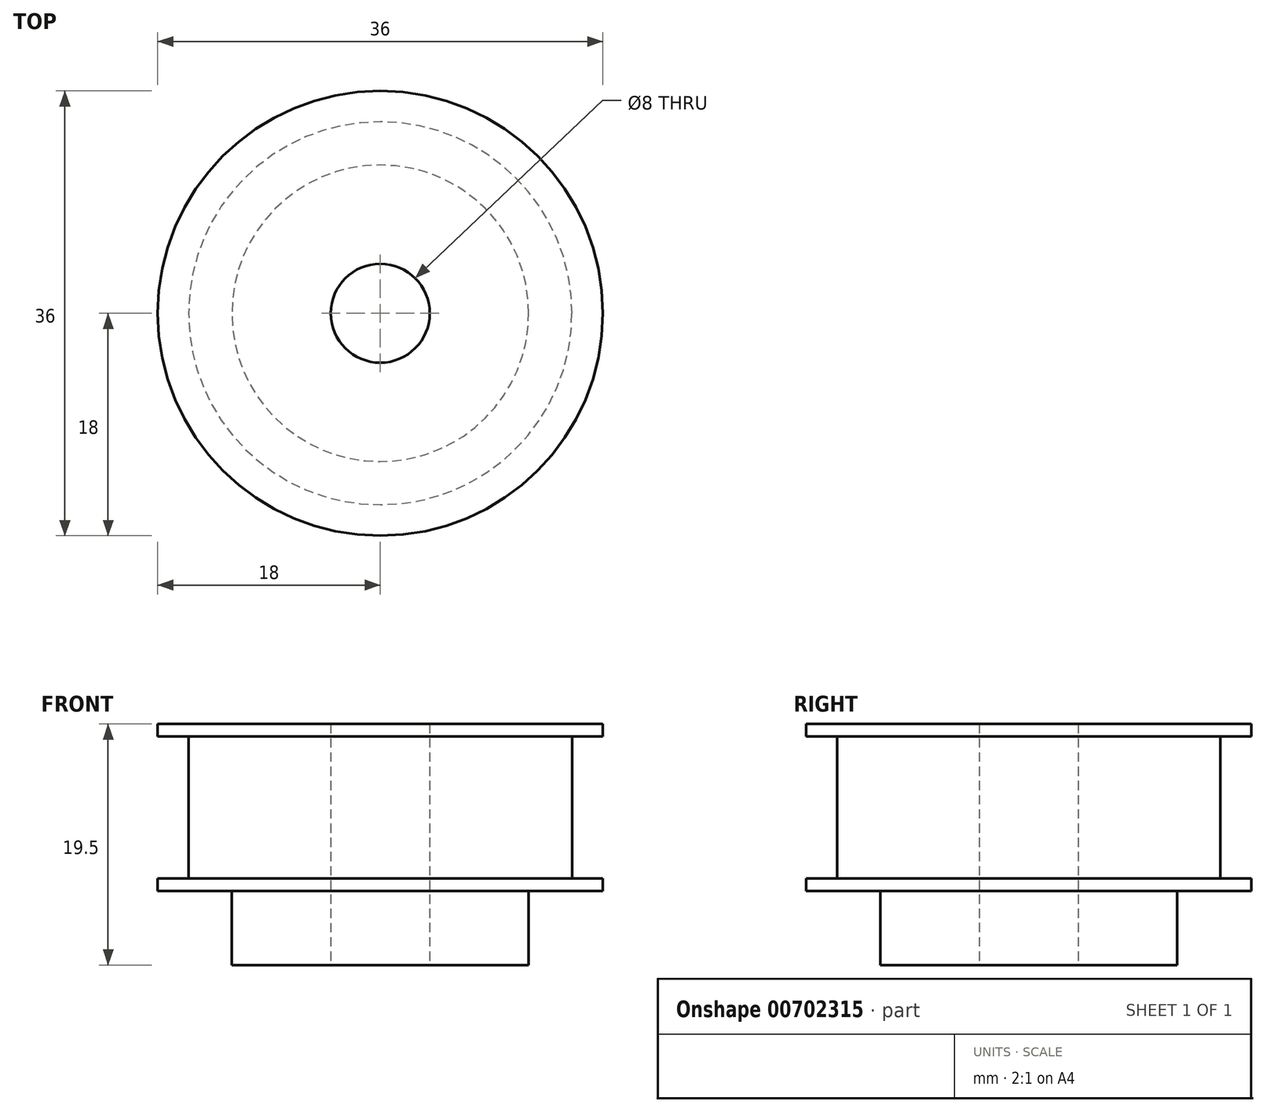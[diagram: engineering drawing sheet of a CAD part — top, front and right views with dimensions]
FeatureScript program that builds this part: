
annotation { "Feature Type Name" : "Feature", "Feature Type Description" : "" }
export const myFeature = defineFeature(function(context is Context, id is Id, definition is map)
    precondition{}
    {
        {
            var Q0;
            Q0=qCreatedBy(makeId("Top.planeOp"),FACE);
            var sketch = newSketch(context, id + "F0", { "sketchPlane" : qUnion([Q0])});
            skCircle(sketch, "E0", {"center": v(0, 0) * mm, "radius": 15.5 * mm});
            skSolve(sketch);
        }
        {
            var Q0;
            Q0 = qSketchRegion(id + "F0", true);
            extrude(context, id + "F1", {"entities" : qUnion([Q0]), "depth" : 11.5 * mm, "offsetDistance" : 25 * mm});
        }
        {
            var Q0;
            Q0=makeQuery(id+"F1.opExtrude","CAP_FACE",FACE,{"disambiguationData":[OSD([sQuery(id+"F0.wireOp",EDGE,"E0")])],"isStart":false});
            var sketch = newSketch(context, id + "F2", { "sketchPlane" : qUnion([Q0])});
            skCircle(sketch, "E1", {"center": v(0, 0) * mm, "radius": 18 * mm});
            skSolve(sketch);
        }
        {
            var Q0;
            Q0 = qSketchRegion(id + "F2", true);
            extrude(context, id + "F3", {"entities" : qUnion([Q0]), "operationType" : NewBodyOperationType.ADD, "depth" : 1 * mm, "offsetDistance" : 25 * mm});
        }
        {
            var Q0;
            Q0=qCreatedBy(makeId("Top.planeOp"),FACE);
            var sketch = newSketch(context, id + "F4", { "sketchPlane" : qUnion([Q0])});
            skCircle(sketch, "E2", {"center": v(0, 0) * mm, "radius": 18 * mm});
            skSolve(sketch);
        }
        {
            var Q0;
            Q0=makeQuery(id+"F4.imprint","IMPRINT",FACE,{"disambiguationData":[TD([[makeQuery(id+"F4.imprint","IMPRINT",EDGE,{"derivedFrom":sQuery(id+"F4.wireOp",EDGE,"E2")}),1.0]])]});
            var Q1;
            Q1=sQuery(id+"F4.wireOp",EDGE,"E2");
            extrude(context, id + "F5", {"entities" : qUnion([Q0]), "operationType" : NewBodyOperationType.ADD, "surfaceEntities" : qUnion([Q1]), "oppositeDirection" : true, "depth" : 1 * mm, "offsetDistance" : 25 * mm});
        }
        {
            var Q0;
            Q0=makeQuery(id+"F5.opExtrude","CAP_FACE",FACE,{"disambiguationData":[OSD([sQuery(id+"F4.wireOp",EDGE,"E2")])],"isStart":false});
            var sketch = newSketch(context, id + "F6", { "sketchPlane" : qUnion([Q0])});
            skCircle(sketch, "E3", {"center": v(0, 0) * mm, "radius": 12 * mm});
            skSolve(sketch);
        }
        {
            var Q0;
            Q0 = qSketchRegion(id + "F6", true);
            extrude(context, id + "F7", {"entities" : qUnion([Q0]), "operationType" : NewBodyOperationType.ADD, "depth" : 6 * mm, "offsetDistance" : 25 * mm});
        }
        {
            var Q0;
            Q0=makeQuery(id+"F7.opExtrude","CAP_FACE",FACE,{"disambiguationData":[OSD([sQuery(id+"F6.wireOp",EDGE,"E3")])],"isStart":false});
            var sketch = newSketch(context, id + "F8", { "sketchPlane" : qUnion([Q0])});
            skCircle(sketch, "E4", {"center": v(0, 0) * mm, "radius": 4 * mm});
            skSolve(sketch);
        }
        {
            var Q0;
            Q0 = qSketchRegion(id + "F8", true);
            extrude(context, id + "F9", {"entities" : qUnion([Q0]), "operationType" : NewBodyOperationType.REMOVE, "endBound" : BoundingType.THROUGH_ALL, "oppositeDirection" : true, "depth" : 25 * mm, "offsetDistance" : 25 * mm});
        }
    });
